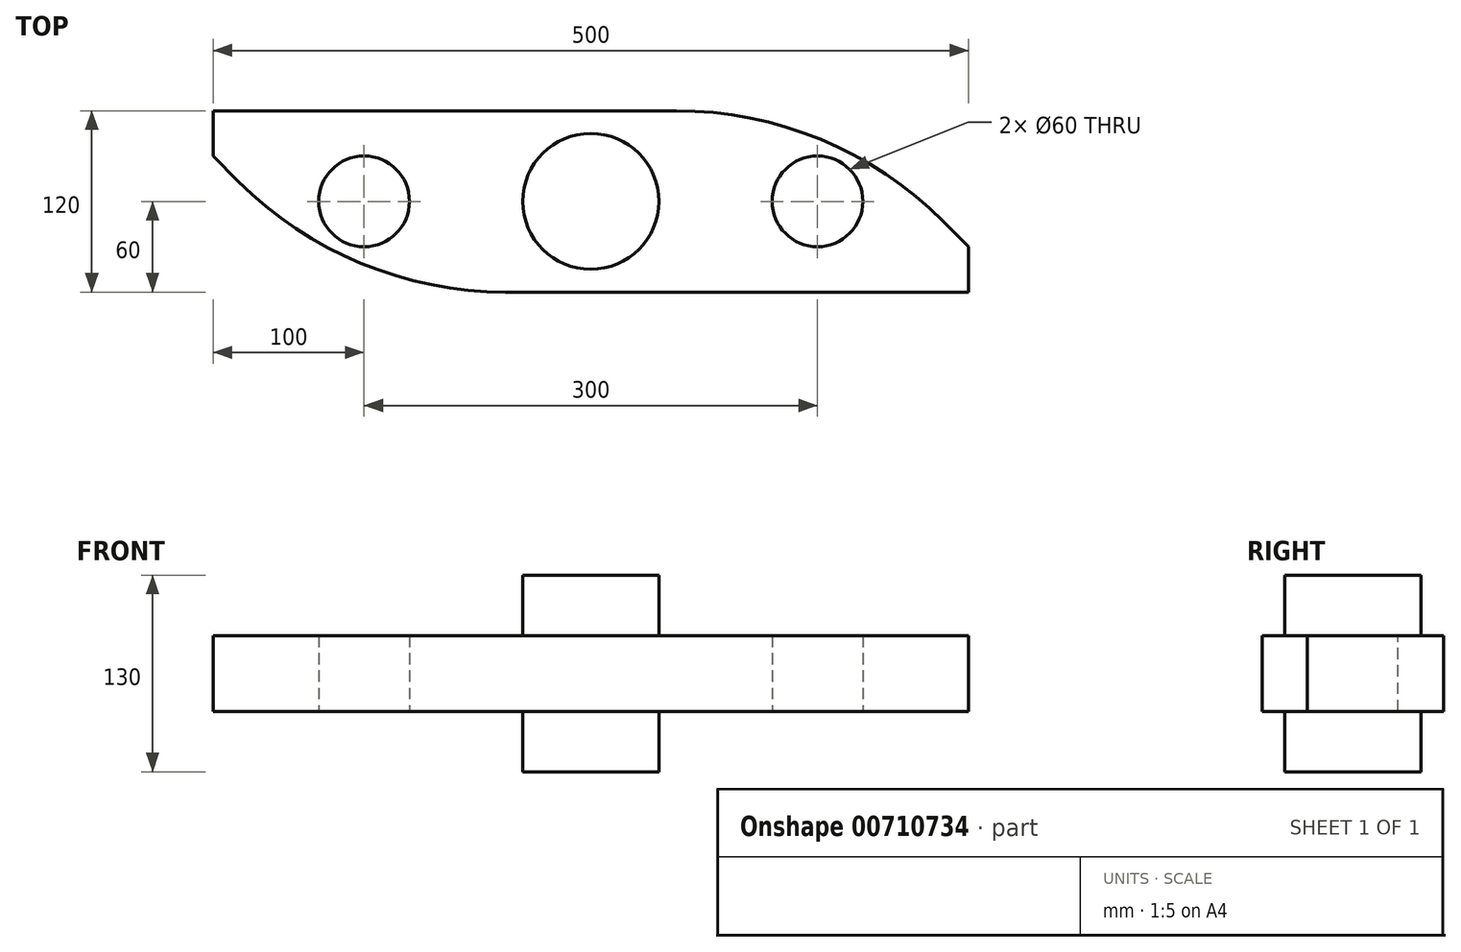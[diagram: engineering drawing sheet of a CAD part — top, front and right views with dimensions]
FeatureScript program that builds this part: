
annotation { "Feature Type Name" : "Feature", "Feature Type Description" : "" }
export const myFeature = defineFeature(function(context is Context, id is Id, definition is map)
    precondition{}
    {
        {
            var Q0;
            Q0=qCreatedBy(makeId("Top.planeOp"),FACE);
            var sketch = newSketch(context, id + "F0", { "sketchPlane" : qUnion([Q0])});
            skLineSegment(sketch, "E0.bottom", {"start": v(250, -60) * mm, "end": v(-250, -60) * mm});
            skLineSegment(sketch, "E0.top", {"start": v(250, 60) * mm, "end": v(-250, 60) * mm});
            skLineSegment(sketch, "E0.left", {"start": v(250, -60) * mm, "end": v(250, 60) * mm});
            skLineSegment(sketch, "E0.right", {"start": v(-250, -60) * mm, "end": v(-250, 60) * mm});
            skPoint(sketch, "E0.middle", {"position": v(0, 0) * mm});
            skCircle(sketch, "E1", {"center": v(-150, 0) * mm, "radius": 30 * mm});
            skCircle(sketch, "E2.1.0.0", {"center": v(150, 0) * mm, "radius": 30 * mm});
            skLineSegment(sketch, "E2.direction1", {"start": v(-150, 0) * mm, "end": v(150, 0) * mm, "construction": true});
            skSolve(sketch);
        }
        {
            var Q0;
            Q0=makeQuery(id+"F0.imprint","IMPRINT",FACE,{"disambiguationData":[TD([[makeQuery(id+"F0.imprint","IMPRINT",EDGE,{"derivedFrom":sQuery(id+"F0.wireOp",EDGE,"E0.bottom")}),-1.0]])]});
            extrude(context, id + "F1", {"entities" : qUnion([Q0]), "endBound" : BoundingType.SYMMETRIC, "depth" : 50 * mm, "offsetDistance" : 25 * mm});
        }
        {
            var Q0;
            Q0=makeQuery(id+"F1.opExtrude","CAP_FACE",FACE,{"disambiguationData":[OSD([sQuery(id+"F0.wireOp",EDGE,"E0.bottom"),sQuery(id+"F0.wireOp",EDGE,"E0.top"),sQuery(id+"F0.wireOp",EDGE,"E0.left"),sQuery(id+"F0.wireOp",EDGE,"E0.right")])],"isStart":false});
            var sketch = newSketch(context, id + "F2", { "sketchPlane" : qUnion([Q0])});
            skCircle(sketch, "E3", {"center": v(0, 0) * mm, "radius": 45 * mm});
            skSolve(sketch);
        }
        {
            var Q0;
            Q0 = qSketchRegion(id + "F2", true);
            extrude(context, id + "F3", {"entities" : qUnion([Q0]), "operationType" : NewBodyOperationType.ADD, "depth" : 40 * mm, "offsetDistance" : 25 * mm, "hasSecondDirection" : true, "secondDirectionOppositeDirection" : true, "secondDirectionDepth" : 90 * mm});
        }
        {
            var Q0;
            Q0=makeQuery(id+"F1.opExtrude","SWEPT_EDGE",EDGE,{"disambiguationData":[OSD([sQuery(id+"F0.wireOp",EDGE,"E0.bottom"),sQuery(id+"F0.wireOp",EDGE,"E0.right")])]});
            var Q1;
            Q1=makeQuery(id+"F1.opExtrude","SWEPT_EDGE",EDGE,{"disambiguationData":[OSD([sQuery(id+"F0.wireOp",EDGE,"E0.top"),sQuery(id+"F0.wireOp",EDGE,"E0.left")])]});
            chamfer(context, id + "F4", {"entities" : qUnion([Q0, Q1]), "width" : 90 * mm, "tangentPropagation" : true});
        }
        {
            var Q0;
            {var subQ0=sQuery(id+"F0.wireOp",EDGE,"E0.bottom");Q0=makeQuery(id+"F4.opChamfer","BLEND_EDGE",EDGE,{"blendedFrom":[makeQuery(id+"F1.opExtrude","SWEPT_EDGE",EDGE,{"disambiguationData":[OSD([subQ0,sQuery(id+"F0.wireOp",EDGE,"E0.right")])]}),makeQuery(id+"F1.opExtrude","SWEPT_FACE",FACE,{"disambiguationData":[OSD([subQ0])]})],"blendedInto":[makeQuery(id+"F1.opExtrude","SWEPT_FACE",FACE,{"disambiguationData":[OSD([subQ0])]})]});}
            var Q1;
            {var subQ0=sQuery(id+"F0.wireOp",EDGE,"E0.top");Q1=makeQuery(id+"F4.opChamfer","BLEND_EDGE",EDGE,{"blendedFrom":[makeQuery(id+"F1.opExtrude","SWEPT_EDGE",EDGE,{"disambiguationData":[OSD([subQ0,sQuery(id+"F0.wireOp",EDGE,"E0.left")])]}),makeQuery(id+"F1.opExtrude","SWEPT_FACE",FACE,{"disambiguationData":[OSD([subQ0])]})],"blendedInto":[makeQuery(id+"F1.opExtrude","SWEPT_FACE",FACE,{"disambiguationData":[OSD([subQ0])]})]});}
            fillet(context, id + "F5", {"entities" : qUnion([Q0, Q1]), "radius" : 250 * mm, "tangentPropagation" : true, "allowEdgeOverflow" : false});
        }
    });
